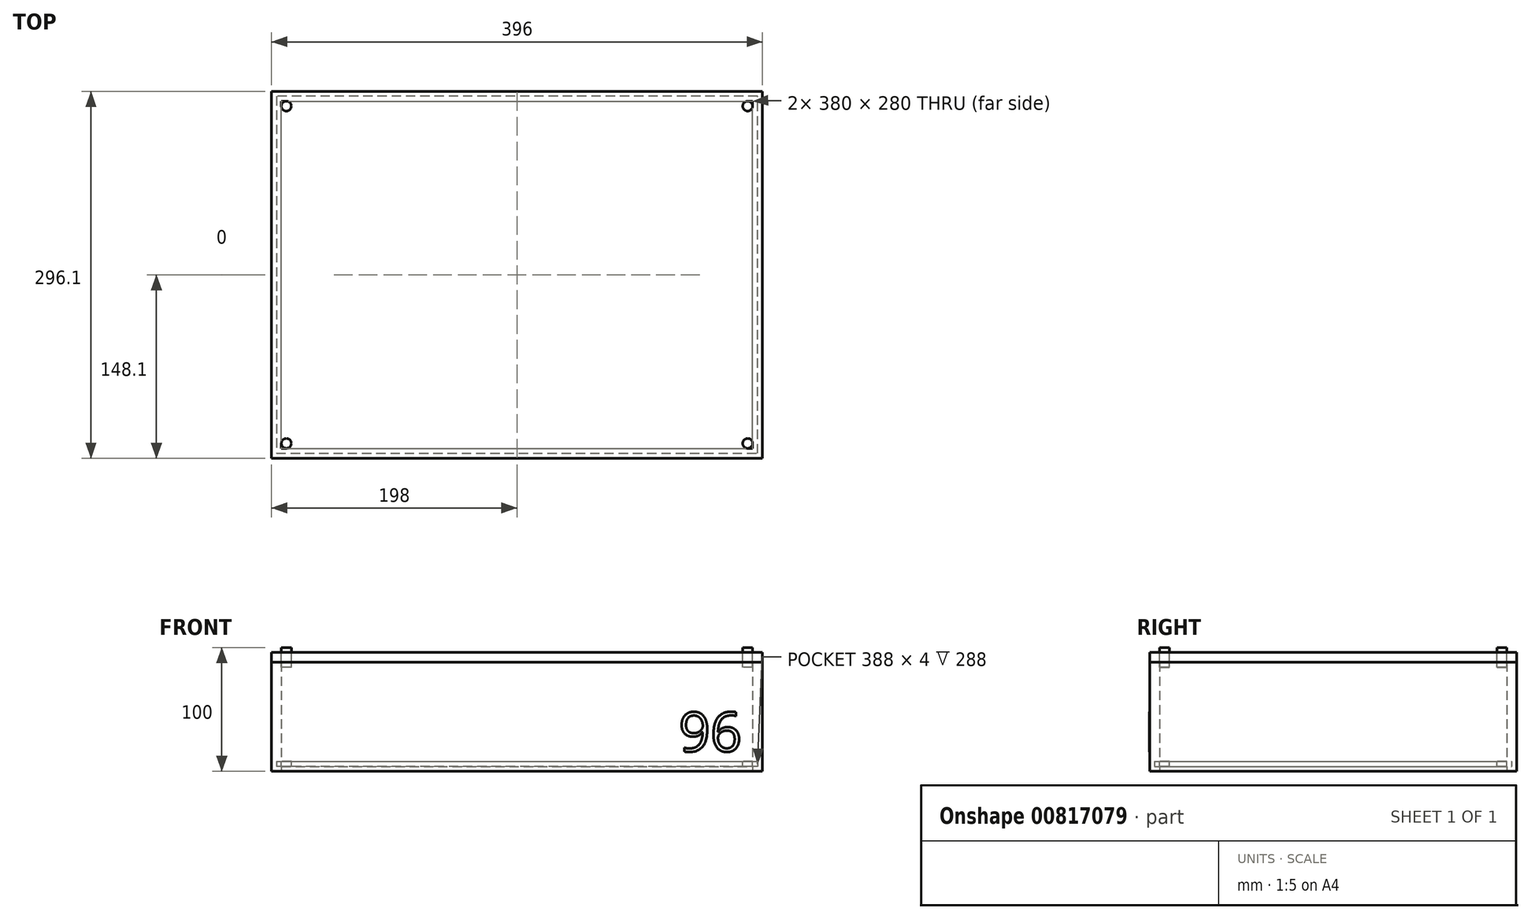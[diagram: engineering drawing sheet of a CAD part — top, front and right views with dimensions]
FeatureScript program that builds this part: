
annotation { "Feature Type Name" : "Feature", "Feature Type Description" : "" }
export const myFeature = defineFeature(function(context is Context, id is Id, definition is map)
    precondition{}
    {
        {
            var Q0;
            Q0=qCreatedBy(makeId("Top.planeOp"),FACE);
            var sketch = newSketch(context, id + "F0", { "sketchPlane" : qUnion([Q0])});
            skLineSegment(sketch, "E0.bottom", {"start": v(0, 0) * mm, "end": v(396, 0) * mm});
            skLineSegment(sketch, "E0.top", {"start": v(0, 296) * mm, "end": v(396, 296) * mm});
            skLineSegment(sketch, "E0.left", {"start": v(0, 0) * mm, "end": v(0, 296) * mm});
            skLineSegment(sketch, "E0.right", {"start": v(396, 0) * mm, "end": v(396, 296) * mm});
            skSolve(sketch);
        }
        {
            var Q0;
            Q0 = qSketchRegion(id + "F0", true);
            extrude(context, id + "F1", {"entities" : qUnion([Q0]), "depth" : (96 - 8) * mm, "offsetDistance" : 25 * mm});
        }
        {
            var Q0;
            Q0=makeQuery(id+"F1.opExtrude","CAP_FACE",FACE,{"disambiguationData":[OSD([sQuery(id+"F0.wireOp",EDGE,"E0.bottom"),sQuery(id+"F0.wireOp",EDGE,"E0.top"),sQuery(id+"F0.wireOp",EDGE,"E0.left"),sQuery(id+"F0.wireOp",EDGE,"E0.right")])],"isStart":false});
            var Q1;
            Q1=makeQuery(id+"F1.opExtrude","CAP_FACE",FACE,{"disambiguationData":[OSD([sQuery(id+"F0.wireOp",EDGE,"E0.bottom"),sQuery(id+"F0.wireOp",EDGE,"E0.top"),sQuery(id+"F0.wireOp",EDGE,"E0.left"),sQuery(id+"F0.wireOp",EDGE,"E0.right")])],"isStart":true});
            shell(context, id + "F2", {"entities" : qUnion([Q0, Q1]), "thickness" : 8 * mm});
        }
        {
            var Q0;
            Q0=qCreatedBy(makeId("Top.planeOp"),FACE);
            cPlane(context, id + "F3", {"entities" : qUnion([Q0]), "cplaneType" : CPlaneType.OFFSET, "offset" : 4 * mm, "width" : 150 * mm, "height" : 150 * mm});
        }
        {
            var Q0;
            Q0=qCreatedBy(id+"F3.planeOp",FACE);
            var sketch = newSketch(context, id + "F4", { "sketchPlane" : qUnion([Q0])});
            skLineSegment(sketch, "E1.0", {"start": v(392, 292) * mm, "end": v(4, 292) * mm});
            skLineSegment(sketch, "E1.1", {"start": v(392, 4) * mm, "end": v(392, 292) * mm});
            skLineSegment(sketch, "E1.2", {"start": v(4, 4) * mm, "end": v(392, 4) * mm});
            skLineSegment(sketch, "E1.3", {"start": v(4, 292) * mm, "end": v(4, 4) * mm});
            skSolve(sketch);
        }
        {
            var Q0;
            Q0 = qSketchRegion(id + "F4", true);
            extrude(context, id + "F5", {"entities" : qUnion([Q0]), "operationType" : NewBodyOperationType.REMOVE, "depth" : 4 * mm, "offsetDistance" : 25 * mm});
        }
        {
            var Q0;
            Q0=makeQuery(id+"F5.boolean.opBoolean","COPY",FACE,{"derivedFrom":makeQuery(id+"F5.opExtrude","CAP_FACE",FACE,{"disambiguationData":[OSD([sQuery(id+"F4.wireOp",EDGE,"E1.0"),sQuery(id+"F4.wireOp",EDGE,"E1.1"),sQuery(id+"F4.wireOp",EDGE,"E1.2"),sQuery(id+"F4.wireOp",EDGE,"E1.3")])],"isStart":true})});
            var sketch = newSketch(context, id + "F6", { "sketchPlane" : qUnion([Q0])});
            skLineSegment(sketch, "E2.0", {"start": v(392, 292) * mm, "end": v(4, 292) * mm});
            skLineSegment(sketch, "E2.1", {"start": v(4, 292) * mm, "end": v(4, 4) * mm});
            skLineSegment(sketch, "E2.2", {"start": v(392, 4) * mm, "end": v(392, 292) * mm});
            skLineSegment(sketch, "E2.3", {"start": v(4, 4) * mm, "end": v(392, 4) * mm});
            skSolve(sketch);
        }
        {
            var Q0;
            Q0=makeQuery(id+"F1.opExtrude","SWEPT_FACE",FACE,{"disambiguationData":[OSD([sQuery(id+"F0.wireOp",EDGE,"E0.bottom")])]});
            var sketch = newSketch(context, id + "F7", { "sketchPlane" : qUnion([Q0])});
            skText(sketch, "E3", { "text": "96", "fontName": "OpenSans-Regular.ttf"});
            const initialGuessF7  = {"E3": [0.32847, 0.016, 1, 0, 0.032]};
            skSetInitialGuess(sketch, initialGuessF7);
            skSolve(sketch);
        }
        {
            var Q0;
            Q0 = qSketchRegion(id + "F7", true);
            extrude(context, id + "F8", {"entities" : qUnion([Q0]), "operationType" : NewBodyOperationType.ADD, "depth" : 0.1 * mm, "offsetDistance" : 25 * mm});
        }
        {
            var Q0;
            Q0 = qSketchRegion(id + "F6", true);
            extrude(context, id + "F9", {"entities" : qUnion([Q0]), "depth" : 4 * mm, "offsetDistance" : 25 * mm});
        }
        {
            var Q0;
            Q0=makeQuery(id+"F1.opExtrude","CAP_FACE",FACE,{"disambiguationData":[OSD([sQuery(id+"F0.wireOp",EDGE,"E0.bottom"),sQuery(id+"F0.wireOp",EDGE,"E0.top"),sQuery(id+"F0.wireOp",EDGE,"E0.left"),sQuery(id+"F0.wireOp",EDGE,"E0.right")])],"isStart":false});
            var sketch = newSketch(context, id + "F10", { "sketchPlane" : qUnion([Q0])});
            skLineSegment(sketch, "E4.0", {"start": v(0, 0) * mm, "end": v(0, 296) * mm});
            skLineSegment(sketch, "E4.1", {"start": v(396, 0) * mm, "end": v(396, 296) * mm});
            skLineSegment(sketch, "E4.2", {"start": v(0, 296) * mm, "end": v(396, 296) * mm});
            skLineSegment(sketch, "E5", {"start": v(0, 0) * mm, "end": v(396, 0) * mm});
            skSolve(sketch);
        }
        {
            var Q0;
            Q0 = qSketchRegion(id + "F10", true);
            extrude(context, id + "F11", {"entities" : qUnion([Q0]), "depth" : 8 * mm, "offsetDistance" : 25 * mm});
        }
        {
            var Q0;
            Q0=makeQuery(id+"F11.opExtrude","CAP_FACE",FACE,{"disambiguationData":[OSD([sQuery(id+"F10.wireOp",EDGE,"E4.0"),sQuery(id+"F10.wireOp",EDGE,"E4.1"),sQuery(id+"F10.wireOp",EDGE,"E4.2"),sQuery(id+"F10.wireOp",EDGE,"E5")])],"isStart":false});
            var sketch = newSketch(context, id + "F12", { "sketchPlane" : qUnion([Q0])});
            skCircle(sketch, "E6", {"center": v(12, 284) * mm, "radius": 4 * mm});
            skCircle(sketch, "E7", {"center": v(12, 12) * mm, "radius": 4 * mm});
            skCircle(sketch, "E8", {"center": v(384, 12) * mm, "radius": 4 * mm});
            skCircle(sketch, "E9", {"center": v(384, 284) * mm, "radius": 4 * mm});
            skSolve(sketch);
        }
        {
            var Q0;
            Q0 = qSketchRegion(id + "F12", true);
            extrude(context, id + "F13", {"entities" : qUnion([Q0]), "operationType" : NewBodyOperationType.REMOVE, "endBound" : BoundingType.THROUGH_ALL, "oppositeDirection" : true, "depth" : 25 * mm, "offsetDistance" : 25 * mm});
        }
        {
            var Q0;
            Q0=makeQuery(id+"F11.opExtrude","CAP_FACE",FACE,{"disambiguationData":[OSD([sQuery(id+"F10.wireOp",EDGE,"E4.0"),sQuery(id+"F10.wireOp",EDGE,"E4.1"),sQuery(id+"F10.wireOp",EDGE,"E4.2"),sQuery(id+"F10.wireOp",EDGE,"E5")])],"isStart":false});
            cPlane(context, id + "F14", {"entities" : qUnion([Q0]), "cplaneType" : CPlaneType.OFFSET, "offset" : 4 * mm, "width" : 150 * mm, "height" : 150 * mm});
        }
        {
            var Q0;
            Q0=qCreatedBy(id+"F14.planeOp",FACE);
            var sketch = newSketch(context, id + "F15", { "sketchPlane" : qUnion([Q0])});
            skCircle(sketch, "E10.0", {"center": v(384, 284) * mm, "radius": 4 * mm});
            skCircle(sketch, "E10.1", {"center": v(384, 12) * mm, "radius": 4 * mm});
            skCircle(sketch, "E10.2", {"center": v(12, 12) * mm, "radius": 4 * mm});
            skCircle(sketch, "E10.3", {"center": v(12, 284) * mm, "radius": 4 * mm});
            skSolve(sketch);
        }
        {
            var Q0;
            Q0 = qSketchRegion(id + "F15", true);
            extrude(context, id + "F16", {"entities" : qUnion([Q0]), "oppositeDirection" : true, "depth" : 16 * mm, "offsetDistance" : 25 * mm});
        }
    });
